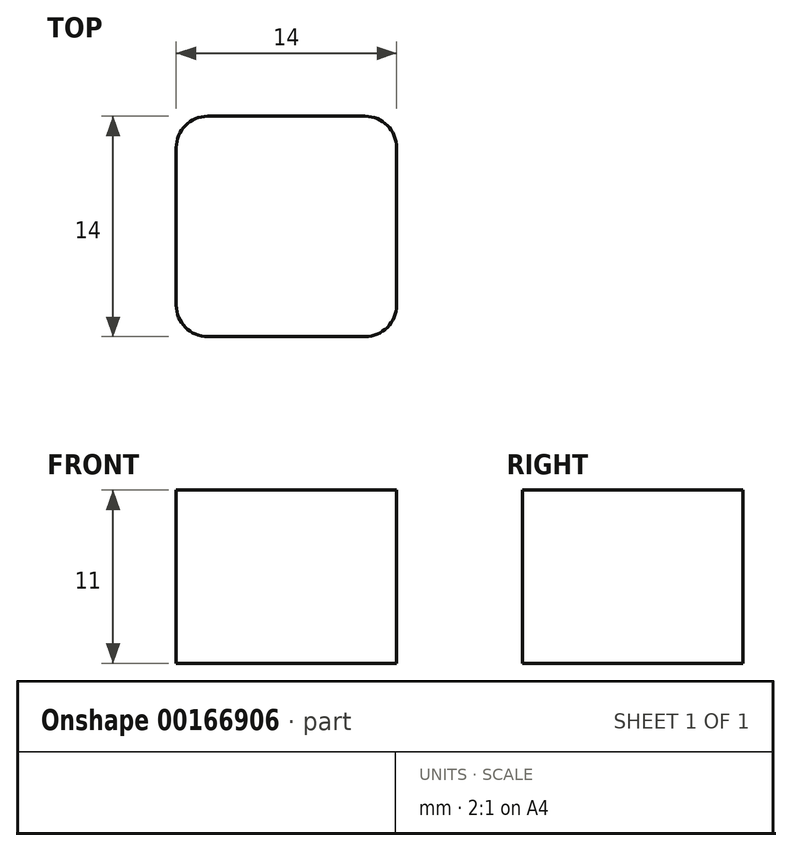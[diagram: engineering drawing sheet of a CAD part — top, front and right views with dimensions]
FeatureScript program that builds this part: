
annotation { "Feature Type Name" : "Feature", "Feature Type Description" : "" }
export const myFeature = defineFeature(function(context is Context, id is Id, definition is map)
    precondition{}
    {
        {
            var Q0;
            Q0=qCreatedBy(makeId("Top.planeOp"),FACE);
            var sketch = newSketch(context, id + "F0", { "sketchPlane" : qUnion([Q0])});
            skLineSegment(sketch, "E0.bottom", {"start": v(5, 7) * mm, "end": v(-5, 7) * mm});
            skLineSegment(sketch, "E0.top", {"start": v(5, -7) * mm, "end": v(-5, -7) * mm});
            skLineSegment(sketch, "E0.left", {"start": v(7, 5) * mm, "end": v(7, -5) * mm});
            skLineSegment(sketch, "E0.right", {"start": v(-7, 5) * mm, "end": v(-7, -5) * mm});
            skPoint(sketch, "E0.middle", {"position": v(0, 0) * mm});
            skPoint(sketch, "E1.visualSharp", {"position": v(-7, 7) * mm});
            skArc(sketch, "E1.filletArc", {"start": v(-5, 7) * mm, "mid": v(-6.41, 6.41) * mm, "end": v(-7, 5) * mm});
            skPoint(sketch, "E2.visualSharp", {"position": v(-7, -7) * mm});
            skArc(sketch, "E2.filletArc", {"start": v(-7, -5) * mm, "mid": v(-6.41, -6.41) * mm, "end": v(-5, -7) * mm});
            skPoint(sketch, "E3.visualSharp", {"position": v(7, -7) * mm});
            skArc(sketch, "E3.filletArc", {"start": v(5, -7) * mm, "mid": v(6.41, -6.41) * mm, "end": v(7, -5) * mm});
            skPoint(sketch, "E4.visualSharp", {"position": v(7, 7) * mm});
            skArc(sketch, "E4.filletArc", {"start": v(7, 5) * mm, "mid": v(6.41, 6.41) * mm, "end": v(5, 7) * mm});
            skSolve(sketch);
        }
        {
            var Q0;
            Q0 = qSketchRegion(id + "F0", true);
            extrude(context, id + "F1", {"entities" : qUnion([Q0]), "depth" : 11 * mm});
        }
    });
